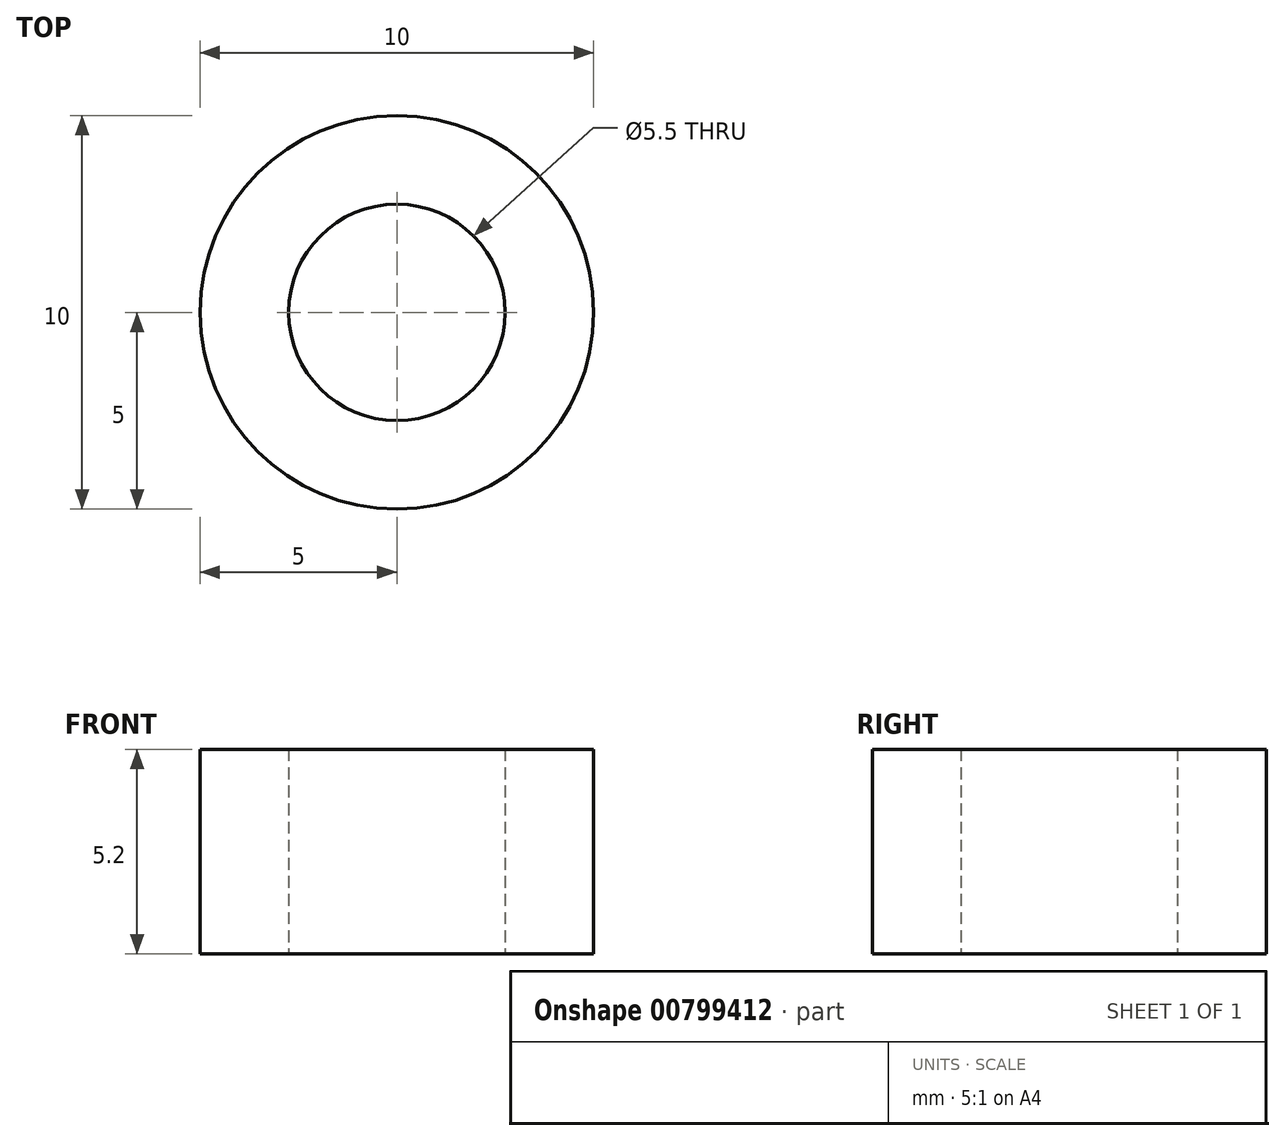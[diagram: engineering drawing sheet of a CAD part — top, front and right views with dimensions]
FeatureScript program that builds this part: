
annotation { "Feature Type Name" : "Feature", "Feature Type Description" : "" }
export const myFeature = defineFeature(function(context is Context, id is Id, definition is map)
    precondition{}
    {
        {
            var Q0;
            Q0=qCreatedBy(makeId("Top.planeOp"),FACE);
            var sketch = newSketch(context, id + "F0", { "sketchPlane" : qUnion([Q0])});
            skCircle(sketch, "E0", {"center": v(0, 0) * mm, "radius": 2.75 * mm});
            skCircle(sketch, "E1", {"center": v(0, 0) * mm, "radius": 5 * mm});
            skSolve(sketch);
        }
        {
            var Q0;
            Q0=makeQuery(id+"F0.imprint","IMPRINT",FACE,{"disambiguationData":[TD([[makeQuery(id+"F0.imprint","IMPRINT",EDGE,{"derivedFrom":sQuery(id+"F0.wireOp",EDGE,"E0")}),-1.0]])]});
            extrude(context, id + "F1", {"entities" : qUnion([Q0]), "depth" : 5.2 * mm, "offsetDistance" : 25 * mm});
        }
    });
